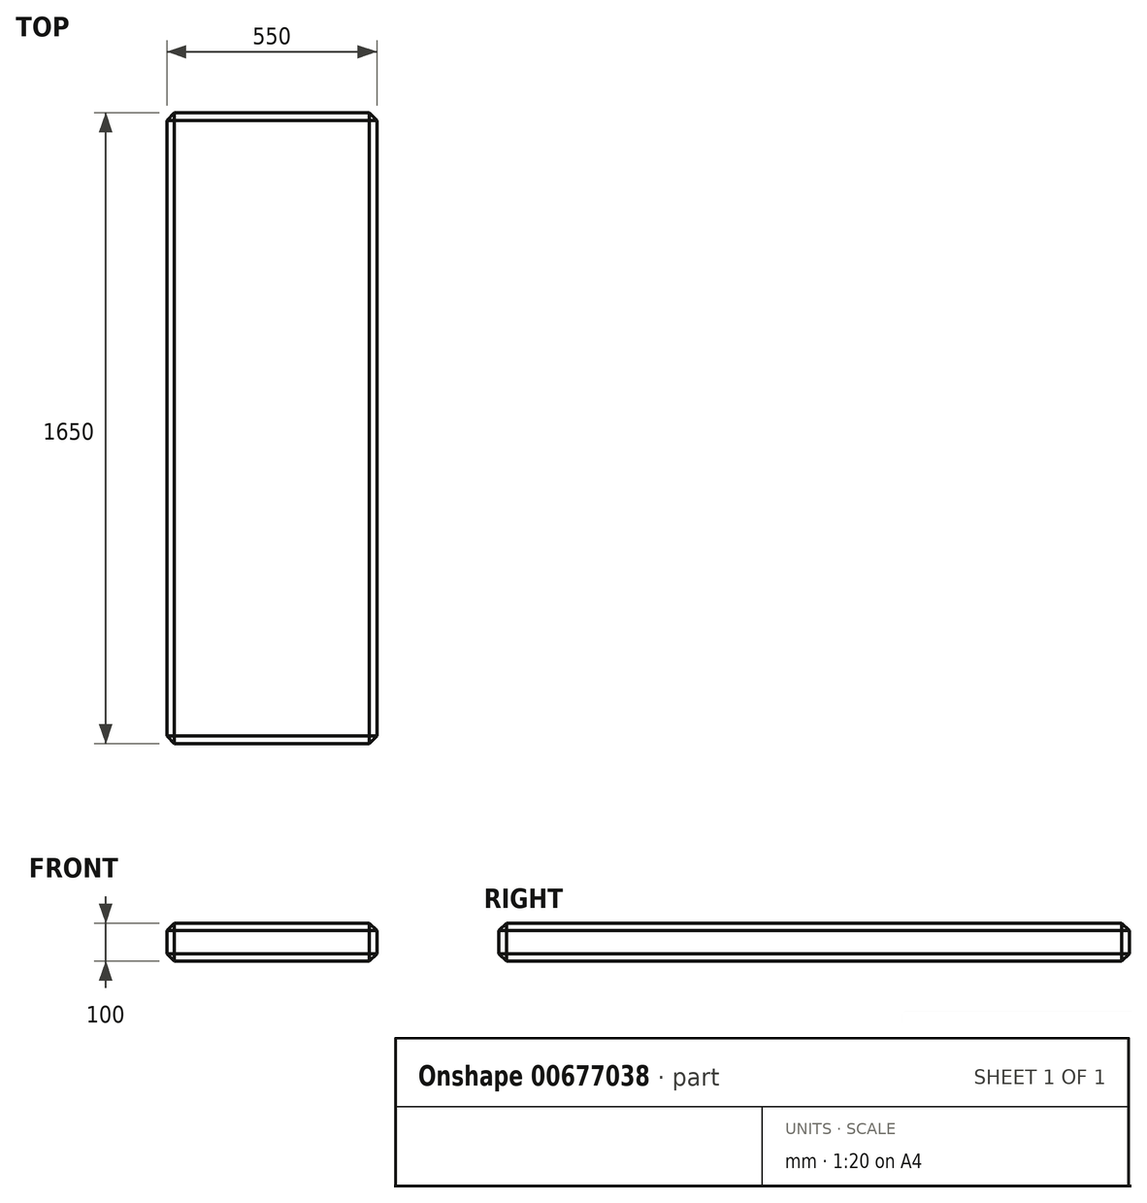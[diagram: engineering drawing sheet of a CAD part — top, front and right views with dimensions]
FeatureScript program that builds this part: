
annotation { "Feature Type Name" : "Feature", "Feature Type Description" : "" }
export const myFeature = defineFeature(function(context is Context, id is Id, definition is map)
    precondition{}
    {
        {
            var Q0;
            Q0=qCreatedBy(makeId("Top.planeOp"),FACE);
            var sketch = newSketch(context, id + "F0", { "sketchPlane" : qUnion([Q0])});
            skLineSegment(sketch, "E0.bottom", {"start": v(-550, 750) * mm, "end": v(0, 750) * mm});
            skLineSegment(sketch, "E0.top", {"start": v(-550, -900) * mm, "end": v(0, -900) * mm});
            skLineSegment(sketch, "E0.left", {"start": v(-550, 750) * mm, "end": v(-550, -900) * mm});
            skLineSegment(sketch, "E0.right", {"start": v(0, 750) * mm, "end": v(0, -900) * mm});
            skSolve(sketch);
        }
        {
            var Q0;
            Q0 = qSketchRegion(id + "F0", true);
            extrude(context, id + "F1", {"entities" : qUnion([Q0]), "depth" : 100 * mm, "offsetDistance" : 25 * mm});
        }
        {
            var Q0;
            Q0=makeQuery(id+"F1.opExtrude","CAP_EDGE",EDGE,{"disambiguationData":[OSD([sQuery(id+"F0.wireOp",EDGE,"E0.left")])],"isStart":false});
            var Q1;
            Q1=makeQuery(id+"F1.opExtrude","CAP_EDGE",EDGE,{"disambiguationData":[OSD([sQuery(id+"F0.wireOp",EDGE,"E0.top")])],"isStart":false});
            var Q2;
            Q2=makeQuery(id+"F1.opExtrude","CAP_EDGE",EDGE,{"disambiguationData":[OSD([sQuery(id+"F0.wireOp",EDGE,"E0.right")])],"isStart":false});
            var Q3;
            Q3=makeQuery(id+"F1.opExtrude","CAP_EDGE",EDGE,{"disambiguationData":[OSD([sQuery(id+"F0.wireOp",EDGE,"E0.bottom")])],"isStart":false});
            var Q4;
            Q4=makeQuery(id+"F1.opExtrude","SWEPT_EDGE",EDGE,{"disambiguationData":[OSD([sQuery(id+"F0.wireOp",EDGE,"E0.top"),sQuery(id+"F0.wireOp",EDGE,"E0.right")])]});
            var Q5;
            Q5=makeQuery(id+"F1.opExtrude","CAP_EDGE",EDGE,{"disambiguationData":[OSD([sQuery(id+"F0.wireOp",EDGE,"E0.right")])],"isStart":true});
            var Q6;
            Q6=makeQuery(id+"F1.opExtrude","CAP_EDGE",EDGE,{"disambiguationData":[OSD([sQuery(id+"F0.wireOp",EDGE,"E0.top")])],"isStart":true});
            var Q7;
            Q7=makeQuery(id+"F1.opExtrude","SWEPT_EDGE",EDGE,{"disambiguationData":[OSD([sQuery(id+"F0.wireOp",EDGE,"E0.top"),sQuery(id+"F0.wireOp",EDGE,"E0.left")])]});
            var Q8;
            Q8=makeQuery(id+"F1.opExtrude","CAP_EDGE",EDGE,{"disambiguationData":[OSD([sQuery(id+"F0.wireOp",EDGE,"E0.left")])],"isStart":true});
            var Q9;
            Q9=makeQuery(id+"F1.opExtrude","SWEPT_EDGE",EDGE,{"disambiguationData":[OSD([sQuery(id+"F0.wireOp",EDGE,"E0.bottom"),sQuery(id+"F0.wireOp",EDGE,"E0.left")])]});
            var Q10;
            Q10=makeQuery(id+"F1.opExtrude","CAP_EDGE",EDGE,{"disambiguationData":[OSD([sQuery(id+"F0.wireOp",EDGE,"E0.bottom")])],"isStart":true});
            var Q11;
            Q11=makeQuery(id+"F1.opExtrude","SWEPT_EDGE",EDGE,{"disambiguationData":[OSD([sQuery(id+"F0.wireOp",EDGE,"E0.bottom"),sQuery(id+"F0.wireOp",EDGE,"E0.right")])]});
            chamfer(context, id + "F2", {"entities" : qUnion([Q0, Q1, Q2, Q3, Q4, Q5, Q6, Q7, Q8, Q9, Q10, Q11]), "width" : 20 * mm, "tangentPropagation" : true});
        }
    });
